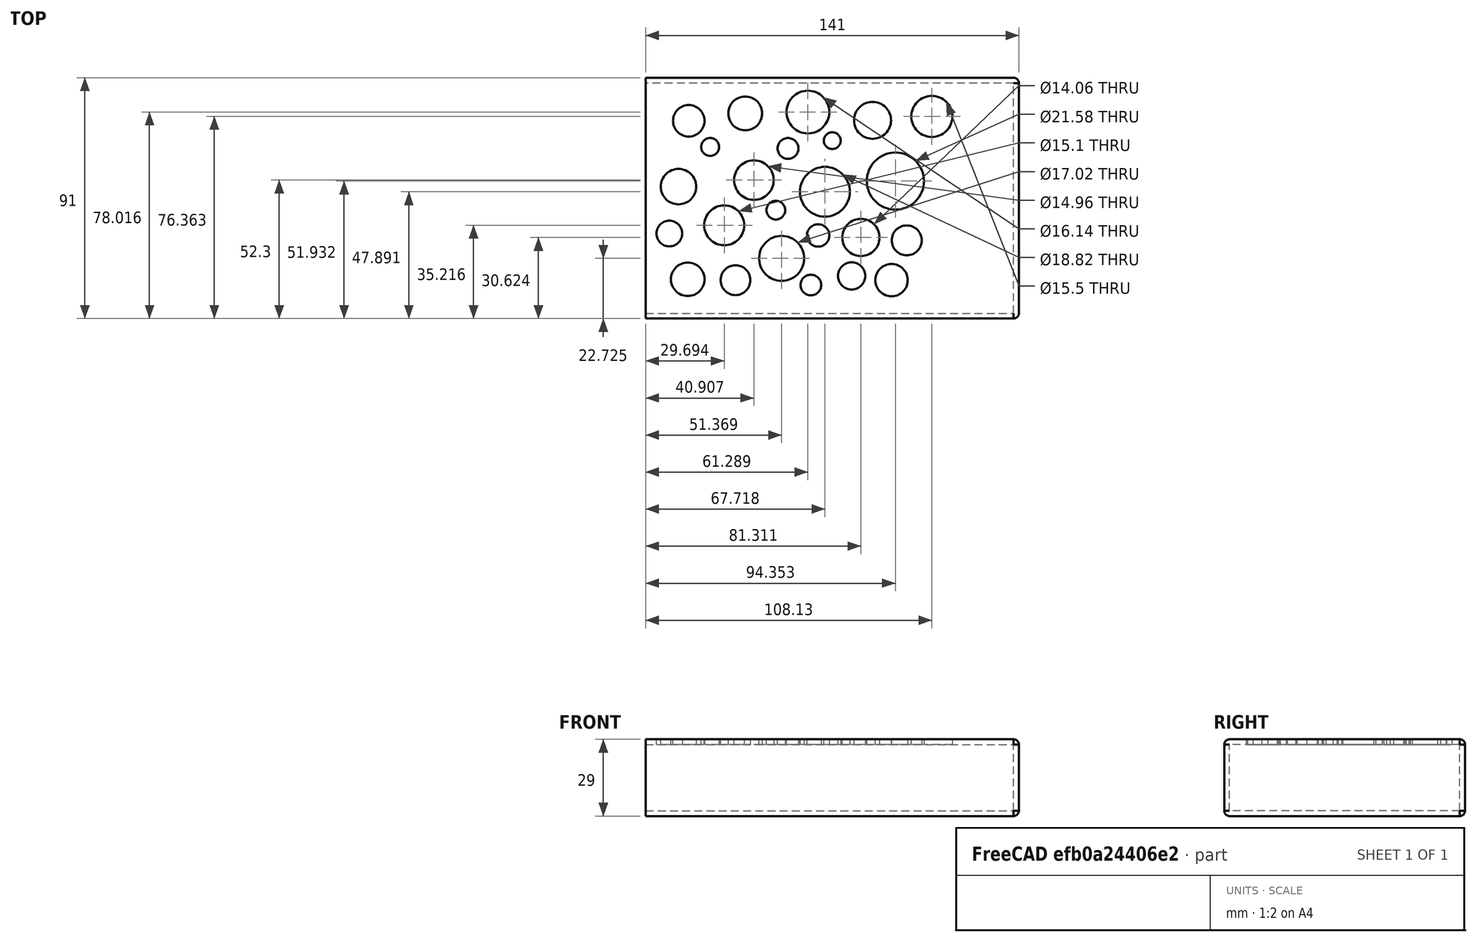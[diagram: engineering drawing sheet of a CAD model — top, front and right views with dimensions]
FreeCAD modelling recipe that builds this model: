
FCSTD DOCUMENT  (FreeCAD 0.18R4 (GitTag))
Label: Biocube Filter V3
License: All rights reserved
LicenseURL: http://en.wikipedia.org/wiki/All_rights_reserved
objects: Sketcher::SketchObject×2, PartDesign::Pad×1, PartDesign::Thickness×1, PartDesign::Pocket×1, PartDesign::Body×1
note: 8 computed .brp shape members not serialized (recipe doc carries the construction recipe); baked Part::Feature solids carry a one-line shape summary decoded from their .brp

FEATURE [Sketcher::SketchObject] Sketch001
  MapMode = 5
  sketch-geometry (4):
    g0: LineSegment StartX=-98.6361 StartY=-57.4943 StartZ=0 EndX=40.3639 EndY=-57.4943 EndZ=0
    g1: LineSegment StartX=40.3639 StartY=-57.4943 StartZ=0 EndX=40.3639 EndY=29.5057 EndZ=0
    g2: LineSegment StartX=40.3639 StartY=29.5057 StartZ=0 EndX=-98.6361 EndY=29.5057 EndZ=0
    g3: LineSegment StartX=-98.6361 StartY=29.5057 StartZ=0 EndX=-98.6361 EndY=-57.4943 EndZ=0
  constraints (10):
    c: Coincident(g0,g1)
    c: Coincident(g1,g2)
    c: Coincident(g2,g3)
    c: Coincident(g3,g0)
    c: Horizontal(g0)
    c: Horizontal(g2)
    c: Vertical(g1)
    c: Vertical(g3)
    c: DistanceY(g0,g1) = 87
    c: DistanceX(g2,g1) = 139
FEATURE [PartDesign::Pad] Pad
  Length = 25
  Length2 = 100
  Profile = -> Sketch001
  Type = 0
FEATURE [PartDesign::Thickness] Thickness
  Base = -> Pad [Face4]
  BaseFeature = -> Pad
  Join = 0
  Mode = 0
  Value = 2
FEATURE [Sketcher::SketchObject] Sketch002
  MapMode = 5
  Placement = pos=(0,0,27) rot=(0,0,1;0rad)
  Support = -> [Thickness]
  sketch-geometry (24):
    g0: Circle CenterX=-82.3346 CenterY=15.2163 CenterZ=0 NormalX=0 NormalY=0 NormalZ=1 AngleXU=0 Radius=5.94705
    g1: Circle CenterX=-61.0213 CenterY=18.0212 CenterZ=0 NormalX=0 NormalY=0 NormalZ=1 AngleXU=0 Radius=6.39154
    g2: Circle CenterX=-57.7329 CenterY=-7.18999 CenterZ=0 NormalX=0 NormalY=0 NormalZ=1 AngleXU=0 Radius=7.47971
    g3: Circle CenterX=-86.2325 CenterY=-9.65631 CenterZ=0 NormalX=0 NormalY=0 NormalZ=1 AngleXU=0 Radius=6.69004
    g4: Circle CenterX=-68.9463 CenterY=-24.274 CenterZ=0 NormalX=0 NormalY=0 NormalZ=1 AngleXU=0 Radius=7.55147
    g5: Circle CenterX=-82.7231 CenterY=-44.6637 CenterZ=0 NormalX=0 NormalY=0 NormalZ=1 AngleXU=0 Radius=6.34199
    g6: Circle CenterX=-47.2707 CenterY=-36.765 CenterZ=0 NormalX=0 NormalY=0 NormalZ=1 AngleXU=0 Radius=8.50949
    g7: Circle CenterX=-30.9222 CenterY=-11.5993 CenterZ=0 NormalX=0 NormalY=0 NormalZ=1 AngleXU=0 Radius=9.40958
    g8: Circle CenterX=-37.3514 CenterY=18.526 CenterZ=0 NormalX=0 NormalY=0 NormalZ=1 AngleXU=0 Radius=8.06988
    g9: Circle CenterX=-17.3291 CenterY=-28.8663 CenterZ=0 NormalX=0 NormalY=0 NormalZ=1 AngleXU=0 Radius=7.03083
    g10: Circle CenterX=-20.8192 CenterY=-43.3779 CenterZ=0 NormalX=0 NormalY=0 NormalZ=1 AngleXU=0 Radius=5.14662
    g11: Circle CenterX=-12.9205 CenterY=15.4033 CenterZ=0 NormalX=0 NormalY=0 NormalZ=1 AngleXU=0 Radius=6.98267
    g12: Circle CenterX=9.48984 CenterY=16.8728 CenterZ=0 NormalX=0 NormalY=0 NormalZ=1 AngleXU=0 Radius=7.75212
    g13: Circle CenterX=-4.28699 CenterY=-7.55813 CenterZ=0 NormalX=0 NormalY=0 NormalZ=1 AngleXU=0 Radius=10.7878
    g14: Circle CenterX=0 CenterY=-29.9684 CenterZ=0 NormalX=0 NormalY=0 NormalZ=1 AngleXU=0 Radius=5.65876
    g15: Circle CenterX=-44.8587 CenterY=4.77725 CenterZ=0 NormalX=0 NormalY=0 NormalZ=1 AngleXU=0 Radius=3.93116
    g16: Circle CenterX=-74.2492 CenterY=5.32832 CenterZ=0 NormalX=0 NormalY=0 NormalZ=1 AngleXU=0 Radius=3.37712
    g17: Circle CenterX=-64.6973 CenterY=-45.003 CenterZ=0 NormalX=0 NormalY=0 NormalZ=1 AngleXU=0 Radius=5.62287
    g18: Circle CenterX=-36.2252 CenterY=-46.84 CenterZ=0 NormalX=0 NormalY=0 NormalZ=1 AngleXU=0 Radius=3.90532
    g19: Circle CenterX=-33.4698 CenterY=-28.1035 CenterZ=0 NormalX=0 NormalY=0 NormalZ=1 AngleXU=0 Radius=4.22889
    g20: Circle CenterX=-49.4509 CenterY=-18.5515 CenterZ=0 NormalX=0 NormalY=0 NormalZ=1 AngleXU=0 Radius=3.52859
    g21: Circle CenterX=-28.1428 CenterY=7.71631 CenterZ=0 NormalX=0 NormalY=0 NormalZ=1 AngleXU=0 Radius=3.16034
    g22: Circle CenterX=-5.73246 CenterY=-45.003 CenterZ=0 NormalX=0 NormalY=0 NormalZ=1 AngleXU=0 Radius=6.10618
    g23: Circle CenterX=-89.6793 CenterY=-27.3687 CenterZ=0 NormalX=0 NormalY=0 NormalZ=1 AngleXU=0 Radius=4.85306
  constraints (1):
    c: PointOnObject(g14,g-2)
FEATURE [PartDesign::Pocket] Pocket
  BaseFeature = -> Thickness
  Length = 5
  Length2 = 100
  Profile = -> Sketch002
  Type = 0
FEATURE [PartDesign::Body] Body001
  Group = -> [Sketch001,Pad,Thickness,Sketch002,Pocket]
  Origin = -> Origin001
  Tip = -> Pocket
